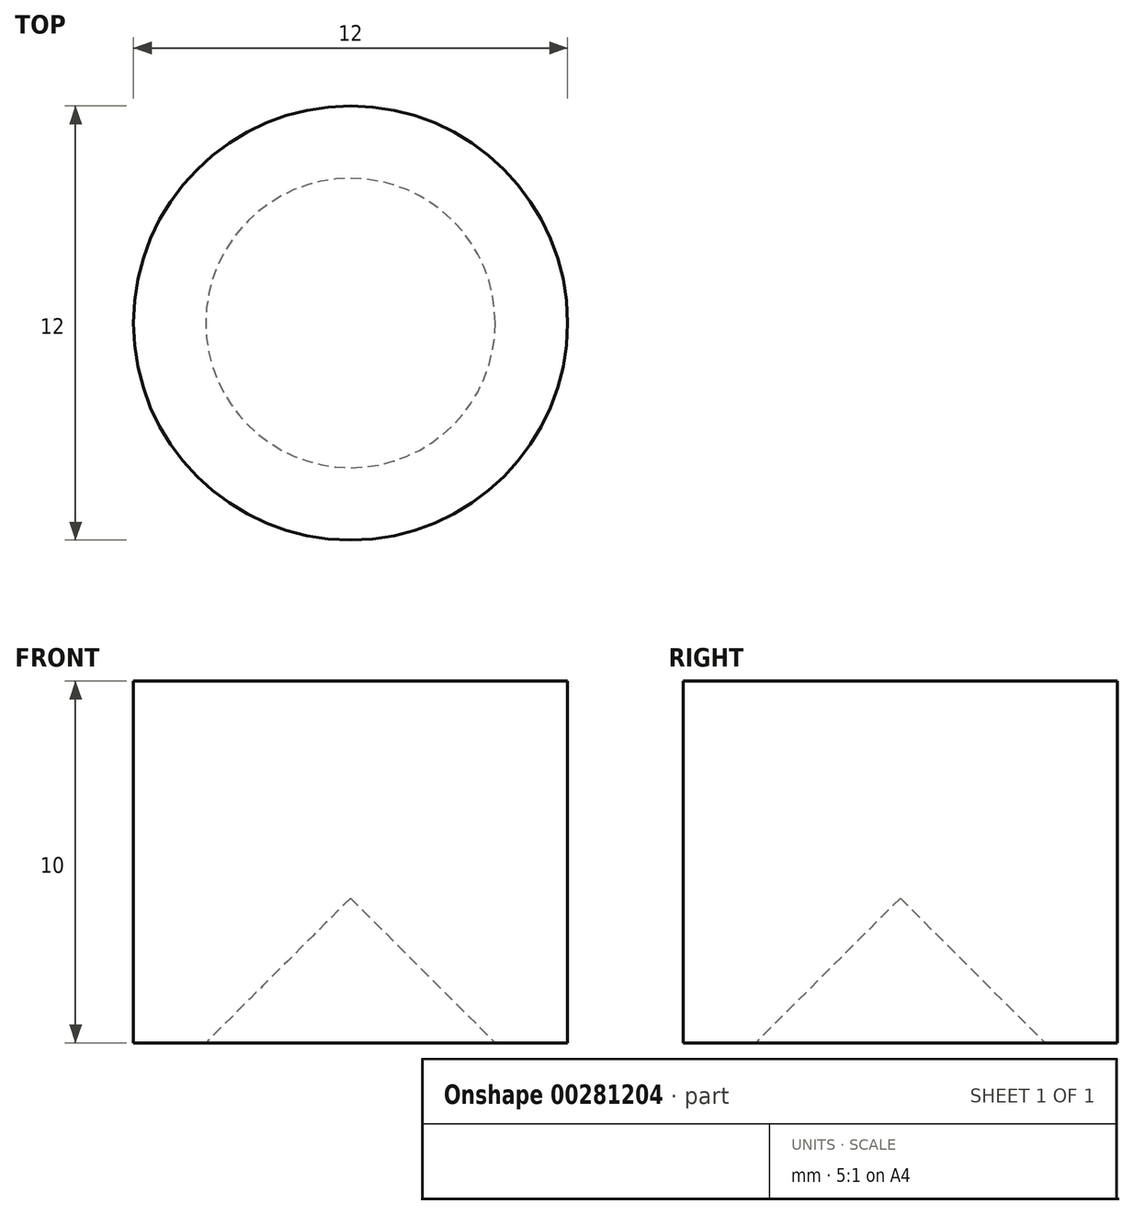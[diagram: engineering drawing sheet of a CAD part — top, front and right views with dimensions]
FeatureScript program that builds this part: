
annotation { "Feature Type Name" : "Feature", "Feature Type Description" : "" }
export const myFeature = defineFeature(function(context is Context, id is Id, definition is map)
    precondition{}
    {
        {
            var Q0;
            Q0=qCreatedBy(makeId("Front.planeOp"),FACE);
            var sketch = newSketch(context, id + "F0", { "sketchPlane" : qUnion([Q0])});
            skLineSegment(sketch, "E0", {"start": v(0, 0) * mm, "end": v(0, 19.12) * mm, "construction": true});
            skLineSegment(sketch, "E1", {"start": v(-6, 0) * mm, "end": v(-6, 10) * mm});
            skLineSegment(sketch, "E2", {"start": v(-6, 10) * mm, "end": v(0, 10) * mm});
            skLineSegment(sketch, "E3", {"start": v(-6, 0) * mm, "end": v(-4, 0) * mm});
            skLineSegment(sketch, "E4", {"start": v(-4, 0) * mm, "end": v(0, 4) * mm});
            skLineSegment(sketch, "E5", {"start": v(0, 4) * mm, "end": v(0, 10) * mm});
            skSolve(sketch);
        }
        {
            var Q0;
            Q0 = qSketchRegion(id + "F0", true);
            var Q1;
            Q1=sQuery(id+"F0.wireOp",EDGE,"E0");
            revolve(context, id + "F1", {"surfaceOperationType" : NewSurfaceOperationType.NEW, "entities" : qUnion([Q0]), "axis" : qUnion([Q1]), "revolveType" : RevolveType.FULL});
        }
    });
